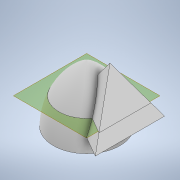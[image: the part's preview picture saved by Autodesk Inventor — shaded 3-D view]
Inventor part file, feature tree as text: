
AUTODESK INVENTOR PART (.ipt)
format: ipt  version: 2022 (Build 260153000, 153)  size: 170,496 bytes
history: native  units: mm
features: other x7, sketch x4, loft x1, revolve x1
ambient origin geometry x8: Origin, YZ Plane, XZ Plane, XY Plane, X Axis, Y Axis, Z Axis, Center Point
bodies: Body1 (feature_tree), Body2 (feature_tree)
feature tree (13):
  other  "Твердое тело1"
  sketch  "Эскиз1"
  sketch  "Эскиз2"
  other  "РабПлоскость1"
  loft  "Лофт1"
  revolve  "Вращение1"
  other  "РабПлоскость2"
  other  "Разделение1"
  sketch  "Эскиз3"
  sketch  "Эскиз7"
  other  "РабПлоскость3"
  other  "Твердое тело2"
  other  "Твердое тело3"
